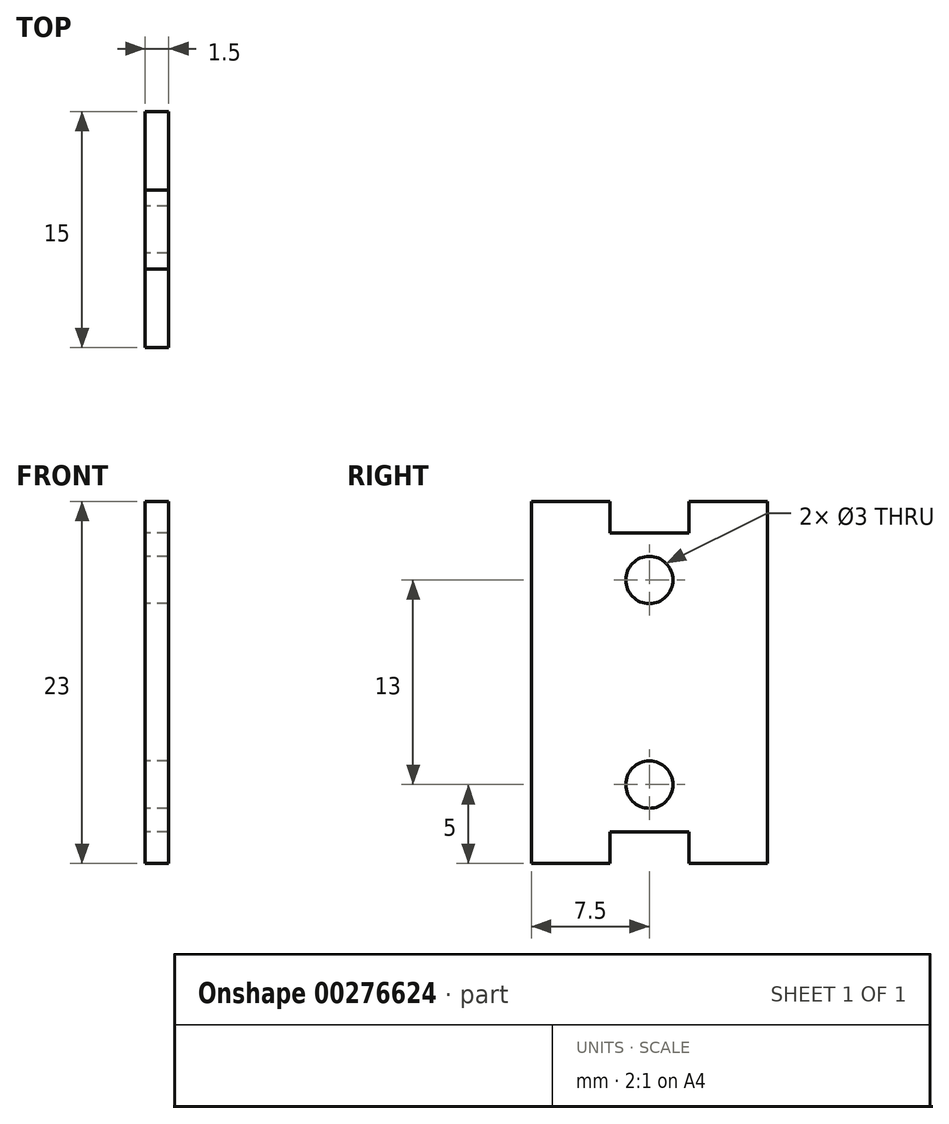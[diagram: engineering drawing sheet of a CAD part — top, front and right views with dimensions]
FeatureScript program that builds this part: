
annotation { "Feature Type Name" : "Feature", "Feature Type Description" : "" }
export const myFeature = defineFeature(function(context is Context, id is Id, definition is map)
    precondition{}
    {
        {
            var Q0;
            Q0=qCreatedBy(makeId("Right.planeOp"),FACE);
            var sketch = newSketch(context, id + "F0", { "sketchPlane" : qUnion([Q0])});
            skLineSegment(sketch, "E0.bottom", {"start": v(7.5, 11.5) * mm, "end": v(-7.5, 11.5) * mm});
            skLineSegment(sketch, "E0.top", {"start": v(7.5, -11.5) * mm, "end": v(-7.5, -11.5) * mm});
            skLineSegment(sketch, "E0.left", {"start": v(7.5, 11.5) * mm, "end": v(7.5, -11.5) * mm});
            skLineSegment(sketch, "E0.right", {"start": v(-7.5, 11.5) * mm, "end": v(-7.5, -11.5) * mm});
            skPoint(sketch, "E0.middle", {"position": v(0, 0) * mm});
            skLineSegment(sketch, "E1", {"start": v(2.5, -11.5) * mm, "end": v(2.5, -9.5) * mm});
            skLineSegment(sketch, "E2", {"start": v(2.5, -9.5) * mm, "end": v(0, -9.5) * mm});
            skLineSegment(sketch, "E3", {"start": v(0, -9.5) * mm, "end": v(0, 0) * mm, "construction": true});
            skLineSegment(sketch, "E4", {"start": v(7.5, 0) * mm, "end": v(0, 0) * mm, "construction": true});
            skLineSegment(sketch, "E5.MirrorCS", {"start": v(-2.5, -9.5) * mm, "end": v(0, -9.5) * mm});
            skLineSegment(sketch, "E6.MirrorCS", {"start": v(-2.5, -11.5) * mm, "end": v(-2.5, -9.5) * mm});
            skLineSegment(sketch, "E7.MirrorCS", {"start": v(-2.5, 11.5) * mm, "end": v(-2.5, 9.5) * mm});
            skLineSegment(sketch, "E8.MirrorCS", {"start": v(-2.5, 9.5) * mm, "end": v(0, 9.5) * mm});
            skLineSegment(sketch, "E9.MirrorCS", {"start": v(2.5, 9.5) * mm, "end": v(0, 9.5) * mm});
            skLineSegment(sketch, "E10.MirrorCS", {"start": v(2.5, 11.5) * mm, "end": v(2.5, 9.5) * mm});
            skCircle(sketch, "E11", {"center": v(0, -6.5) * mm, "radius": 1.5 * mm});
            skCircle(sketch, "E12.MirrorC", {"center": v(0, 6.5) * mm, "radius": 1.5 * mm});
            skSolve(sketch);
        }
        {
            var Q0;
            {var subQ4=sQuery(id+"F0.wireOp",EDGE,"E0.left");Q0=makeQuery(id+"F0.imprint","IMPRINT",FACE,{"disambiguationData":[TD([[makeQuery(id+"F0.imprint","IMPRINT",EDGE,{"derivedFrom":subQ4}),-1.0]])]});}
            extrude(context, id + "F1", {"entities" : qUnion([Q0]), "depth" : 1.5 * mm});
        }
    });
